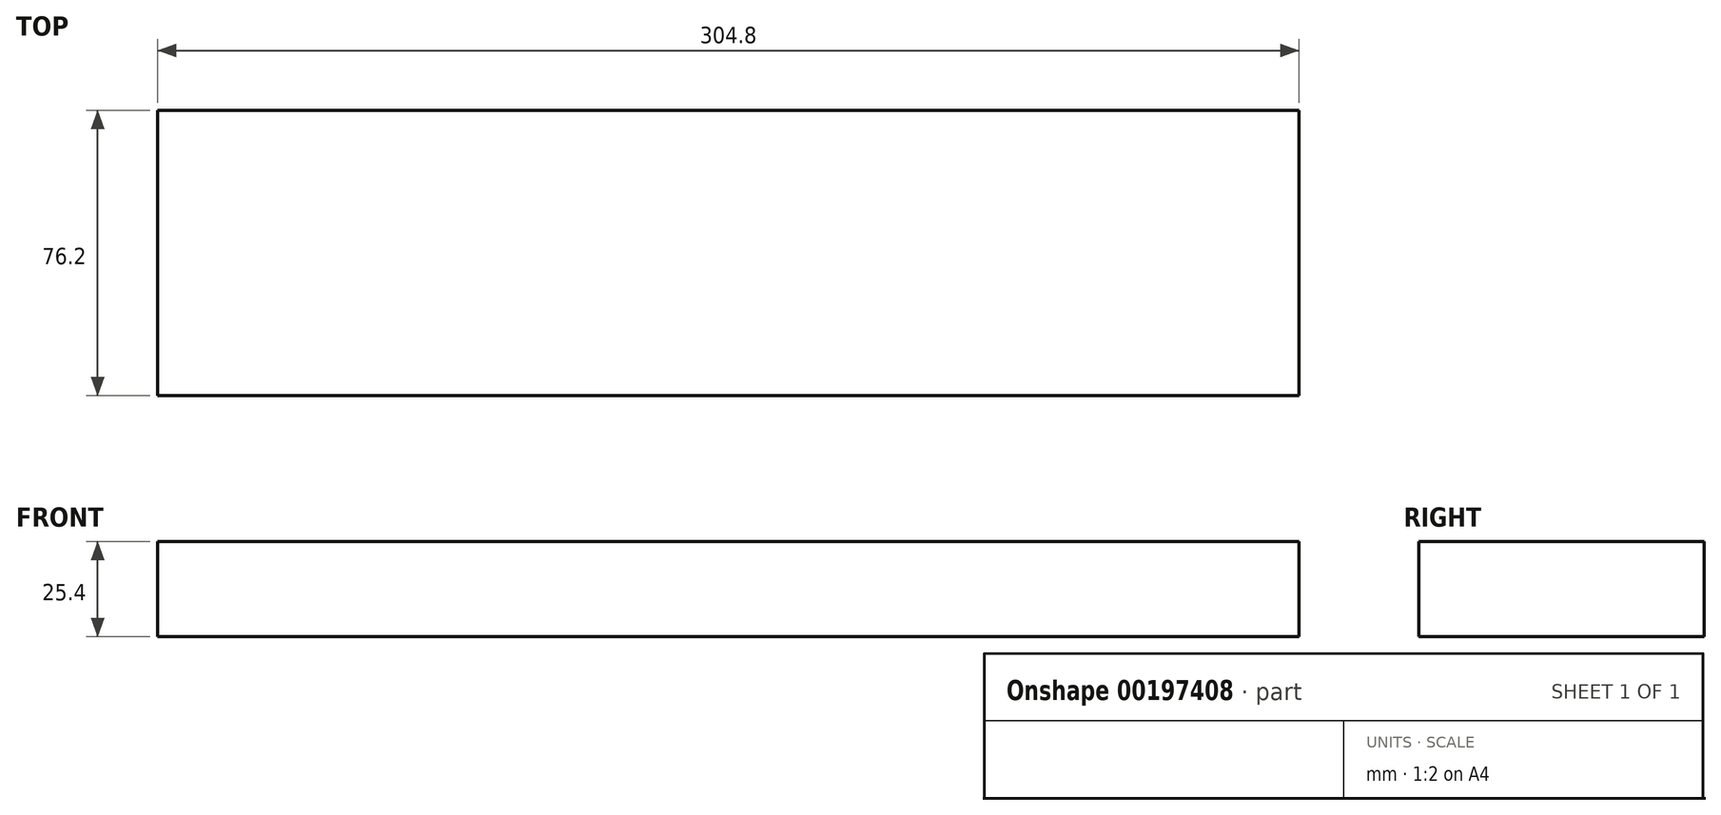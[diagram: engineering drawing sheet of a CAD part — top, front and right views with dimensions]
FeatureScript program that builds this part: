
annotation { "Feature Type Name" : "Feature", "Feature Type Description" : "" }
export const myFeature = defineFeature(function(context is Context, id is Id, definition is map)
    precondition{}
    {
        {
            var Q0;
            Q0=qCreatedBy(makeId("Top.planeOp"),FACE);
            var sketch = newSketch(context, id + "F0", { "sketchPlane" : qUnion([Q0])});
            skLineSegment(sketch, "E0.bottom", {"start": v(-38.1, 38.1) * mm, "end": v(266.7, 38.1) * mm});
            skLineSegment(sketch, "E0.top", {"start": v(-38.1, -38.1) * mm, "end": v(266.7, -38.1) * mm});
            skLineSegment(sketch, "E0.left", {"start": v(-38.1, 38.1) * mm, "end": v(-38.1, -38.1) * mm});
            skLineSegment(sketch, "E0.right", {"start": v(266.7, 38.1) * mm, "end": v(266.7, -38.1) * mm});
            skSolve(sketch);
        }
        {
            var Q0;
            Q0 = qSketchRegion(id + "F0", true);
            extrude(context, id + "F1", {"entities" : qUnion([Q0]), "depth" : 25.4 * mm});
        }
    });
